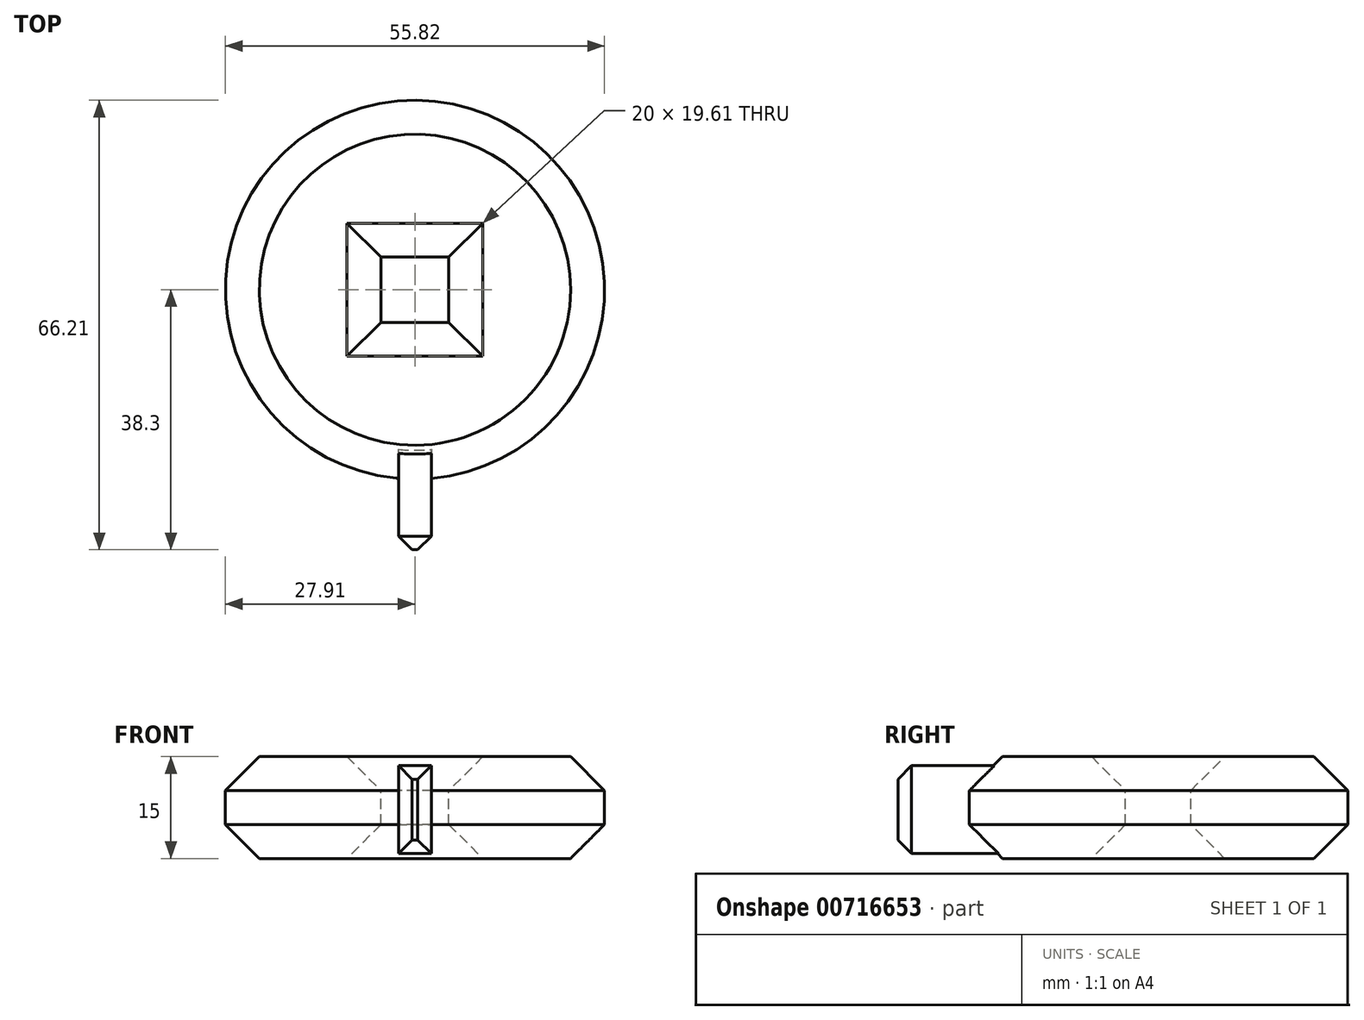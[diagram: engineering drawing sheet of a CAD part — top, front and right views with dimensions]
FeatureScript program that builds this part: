
annotation { "Feature Type Name" : "Feature", "Feature Type Description" : "" }
export const myFeature = defineFeature(function(context is Context, id is Id, definition is map)
    precondition{}
    {
        {
            var Q0;
            Q0=qCreatedBy(makeId("Top.planeOp"),FACE);
            var sketch = newSketch(context, id + "F0", { "sketchPlane" : qUnion([Q0])});
            skCircle(sketch, "E0", {"center": v(0, 0) * mm, "radius": 27.91 * mm});
            skSolve(sketch);
        }
        {
            var Q0;
            Q0=makeQuery(id+"F0.imprint","IMPRINT",FACE,{"disambiguationData":[TD([[makeQuery(id+"F0.imprint","IMPRINT",EDGE,{"derivedFrom":sQuery(id+"F0.wireOp",EDGE,"E0")}),1.0]])]});
            extrude(context, id + "F1", {"entities" : qUnion([Q0]), "depth" : 15 * mm, "offsetDistance" : 25 * mm});
        }
        {
            var Q0;
            Q0=makeQuery(id+"F1.opExtrude","CAP_FACE",FACE,{"disambiguationData":[OSD([sQuery(id+"F0.wireOp",EDGE,"E0")])],"isStart":false});
            var sketch = newSketch(context, id + "F2", { "sketchPlane" : qUnion([Q0])});
            skLineSegment(sketch, "E1.bottom", {"start": v(5, 4.8) * mm, "end": v(-5, 4.8) * mm});
            skLineSegment(sketch, "E1.top", {"start": v(5, -4.8) * mm, "end": v(-5, -4.8) * mm});
            skLineSegment(sketch, "E1.left", {"start": v(5, 4.8) * mm, "end": v(5, -4.8) * mm});
            skLineSegment(sketch, "E1.right", {"start": v(-5, 4.8) * mm, "end": v(-5, -4.8) * mm});
            skPoint(sketch, "E1.middle", {"position": v(0, 0) * mm});
            skSolve(sketch);
        }
        {
            var Q0;
            Q0=makeQuery(id+"F2.imprint","IMPRINT",FACE,{"disambiguationData":[TD([[makeQuery(id+"F2.imprint","IMPRINT",EDGE,{"derivedFrom":sQuery(id+"F2.wireOp",EDGE,"E1.bottom")}),1.0]])]});
            extrude(context, id + "F3", {"entities" : qUnion([Q0]), "operationType" : NewBodyOperationType.REMOVE, "oppositeDirection" : true, "depth" : 25 * mm, "offsetDistance" : 25 * mm});
        }
        {
            var Q0;
            Q0=qCreatedBy(makeId("Front.planeOp"),FACE);
            cPlane(context, id + "F4", {"entities" : qUnion([Q0]), "cplaneType" : CPlaneType.OFFSET, "offset" : 28.3 * mm, "width" : 150 * mm, "height" : 150 * mm});
        }
        {
            var Q0;
            Q0=qCreatedBy(id+"F4.planeOp",FACE);
            var sketch = newSketch(context, id + "F5", { "sketchPlane" : qUnion([Q0])});
            skLineSegment(sketch, "E2.bottom", {"start": v(2.4, 13.68) * mm, "end": v(-2.4, 13.68) * mm});
            skLineSegment(sketch, "E2.top", {"start": v(2.4, 0.73) * mm, "end": v(-2.4, 0.73) * mm});
            skLineSegment(sketch, "E2.left", {"start": v(2.4, 13.68) * mm, "end": v(2.4, 0.73) * mm});
            skLineSegment(sketch, "E2.right", {"start": v(-2.4, 13.68) * mm, "end": v(-2.4, 0.73) * mm});
            skPoint(sketch, "E2.middle", {"position": v(0, 7.2) * mm});
            skSolve(sketch);
        }
        {
            var Q0;
            Q0=makeQuery(id+"F5.imprint","IMPRINT",FACE,{"disambiguationData":[TD([[makeQuery(id+"F5.imprint","IMPRINT",EDGE,{"derivedFrom":sQuery(id+"F5.wireOp",EDGE,"E2.bottom")}),1.0]])]});
            extrude(context, id + "F6", {"entities" : qUnion([Q0]), "operationType" : NewBodyOperationType.ADD, "depth" : 10 * mm, "offsetDistance" : 25 * mm, "hasSecondDirection" : true, "secondDirectionOppositeDirection" : true, "secondDirectionDepth" : 5 * mm});
        }
        {
            var Q0;
            Q0=makeQuery(id+"F3.boolean.opBoolean","COPY",EDGE,{"derivedFrom":makeQuery(id+"F3.opExtrude","CAP_EDGE",EDGE,{"disambiguationData":[OSD([sQuery(id+"F2.wireOp",EDGE,"E1.bottom")])],"isStart":true})});
            var Q1;
            Q1=makeQuery(id+"F3.boolean.opBoolean","COPY",EDGE,{"derivedFrom":makeQuery(id+"F3.opExtrude","CAP_EDGE",EDGE,{"disambiguationData":[OSD([sQuery(id+"F2.wireOp",EDGE,"E1.left")])],"isStart":true})});
            var Q2;
            Q2=makeQuery(id+"F3.boolean.opBoolean","COPY",EDGE,{"derivedFrom":makeQuery(id+"F3.opExtrude","CAP_EDGE",EDGE,{"disambiguationData":[OSD([sQuery(id+"F2.wireOp",EDGE,"E1.top")])],"isStart":true})});
            var Q3;
            Q3=makeQuery(id+"F3.boolean.opBoolean","COPY",EDGE,{"derivedFrom":makeQuery(id+"F3.opExtrude","CAP_EDGE",EDGE,{"disambiguationData":[OSD([sQuery(id+"F2.wireOp",EDGE,"E1.right")])],"isStart":true})});
            var Q4;
            Q4=makeQuery(id+"F1.opExtrude","CAP_FACE",FACE,{"disambiguationData":[OSD([sQuery(id+"F0.wireOp",EDGE,"E0")])],"isStart":false});
            var Q5;
            Q5=makeQuery(id+"F1.opExtrude","CAP_FACE",FACE,{"disambiguationData":[OSD([sQuery(id+"F0.wireOp",EDGE,"E0")])],"isStart":true});
            chamfer(context, id + "F7", {"entities" : qUnion([Q0, Q1, Q2, Q3, Q4, Q5]), "width" : 5 * mm, "tangentPropagation" : true});
        }
        {
            var Q0;
            Q0=makeQuery(id+"Fkjk2feS8p6Myqn_2.8.F6.opExtrude","CAP_FACE",FACE,{"disambiguationData":[OSD([sQuery(id+"F5.wireOp",EDGE,"E2.bottom"),sQuery(id+"F5.wireOp",EDGE,"E2.top"),sQuery(id+"F5.wireOp",EDGE,"E2.left"),sQuery(id+"F5.wireOp",EDGE,"E2.right")])],"isStart":false});
            var Q1;
            Q1=makeQuery(id+"Fkjk2feS8p6Myqn_2.7.F6.opExtrude","CAP_FACE",FACE,{"disambiguationData":[OSD([sQuery(id+"F5.wireOp",EDGE,"E2.bottom"),sQuery(id+"F5.wireOp",EDGE,"E2.top"),sQuery(id+"F5.wireOp",EDGE,"E2.left"),sQuery(id+"F5.wireOp",EDGE,"E2.right")])],"isStart":false});
            var Q2;
            Q2=makeQuery(id+"Fkjk2feS8p6Myqn_2.6.F6.opExtrude","CAP_FACE",FACE,{"disambiguationData":[OSD([sQuery(id+"F5.wireOp",EDGE,"E2.bottom"),sQuery(id+"F5.wireOp",EDGE,"E2.top"),sQuery(id+"F5.wireOp",EDGE,"E2.left"),sQuery(id+"F5.wireOp",EDGE,"E2.right")])],"isStart":false});
            var Q3;
            Q3=makeQuery(id+"Fkjk2feS8p6Myqn_2.9.F6.opExtrude","CAP_FACE",FACE,{"disambiguationData":[OSD([sQuery(id+"F5.wireOp",EDGE,"E2.bottom"),sQuery(id+"F5.wireOp",EDGE,"E2.top"),sQuery(id+"F5.wireOp",EDGE,"E2.left"),sQuery(id+"F5.wireOp",EDGE,"E2.right")])],"isStart":false});
            var Q4;
            Q4=makeQuery(id+"Fkjk2feS8p6Myqn_2.10.F6.opExtrude","CAP_FACE",FACE,{"disambiguationData":[OSD([sQuery(id+"F5.wireOp",EDGE,"E2.bottom"),sQuery(id+"F5.wireOp",EDGE,"E2.top"),sQuery(id+"F5.wireOp",EDGE,"E2.left"),sQuery(id+"F5.wireOp",EDGE,"E2.right")])],"isStart":false});
            var Q5;
            Q5=makeQuery(id+"Fkjk2feS8p6Myqn_2.11.F6.opExtrude","CAP_FACE",FACE,{"disambiguationData":[OSD([sQuery(id+"F5.wireOp",EDGE,"E2.bottom"),sQuery(id+"F5.wireOp",EDGE,"E2.top"),sQuery(id+"F5.wireOp",EDGE,"E2.left"),sQuery(id+"F5.wireOp",EDGE,"E2.right")])],"isStart":false});
            var Q6;
            Q6=makeQuery(id+"F6.opExtrude","CAP_FACE",FACE,{"disambiguationData":[OSD([sQuery(id+"F5.wireOp",EDGE,"E2.bottom"),sQuery(id+"F5.wireOp",EDGE,"E2.top"),sQuery(id+"F5.wireOp",EDGE,"E2.left"),sQuery(id+"F5.wireOp",EDGE,"E2.right")])],"isStart":false});
            var Q7;
            Q7=makeQuery(id+"Fkjk2feS8p6Myqn_2.1.F6.opExtrude","CAP_FACE",FACE,{"disambiguationData":[OSD([sQuery(id+"F5.wireOp",EDGE,"E2.bottom"),sQuery(id+"F5.wireOp",EDGE,"E2.top"),sQuery(id+"F5.wireOp",EDGE,"E2.left"),sQuery(id+"F5.wireOp",EDGE,"E2.right")])],"isStart":false});
            var Q8;
            Q8=makeQuery(id+"Fkjk2feS8p6Myqn_2.2.F6.opExtrude","CAP_FACE",FACE,{"disambiguationData":[OSD([sQuery(id+"F5.wireOp",EDGE,"E2.bottom"),sQuery(id+"F5.wireOp",EDGE,"E2.top"),sQuery(id+"F5.wireOp",EDGE,"E2.left"),sQuery(id+"F5.wireOp",EDGE,"E2.right")])],"isStart":false});
            var Q9;
            Q9=makeQuery(id+"Fkjk2feS8p6Myqn_2.3.F6.opExtrude","CAP_FACE",FACE,{"disambiguationData":[OSD([sQuery(id+"F5.wireOp",EDGE,"E2.bottom"),sQuery(id+"F5.wireOp",EDGE,"E2.top"),sQuery(id+"F5.wireOp",EDGE,"E2.left"),sQuery(id+"F5.wireOp",EDGE,"E2.right")])],"isStart":false});
            var Q10;
            Q10=makeQuery(id+"Fkjk2feS8p6Myqn_2.4.F6.opExtrude","CAP_FACE",FACE,{"disambiguationData":[OSD([sQuery(id+"F5.wireOp",EDGE,"E2.bottom"),sQuery(id+"F5.wireOp",EDGE,"E2.top"),sQuery(id+"F5.wireOp",EDGE,"E2.left"),sQuery(id+"F5.wireOp",EDGE,"E2.right")])],"isStart":false});
            var Q11;
            Q11=makeQuery(id+"Fkjk2feS8p6Myqn_2.5.F6.opExtrude","CAP_FACE",FACE,{"disambiguationData":[OSD([sQuery(id+"F5.wireOp",EDGE,"E2.bottom"),sQuery(id+"F5.wireOp",EDGE,"E2.top"),sQuery(id+"F5.wireOp",EDGE,"E2.left"),sQuery(id+"F5.wireOp",EDGE,"E2.right")])],"isStart":false});
            chamfer(context, id + "F8", {"entities" : qUnion([Q0, Q1, Q2, Q3, Q4, Q5, Q6, Q7, Q8, Q9, Q10, Q11]), "width" : 2 * mm, "tangentPropagation" : true});
        }
    });
